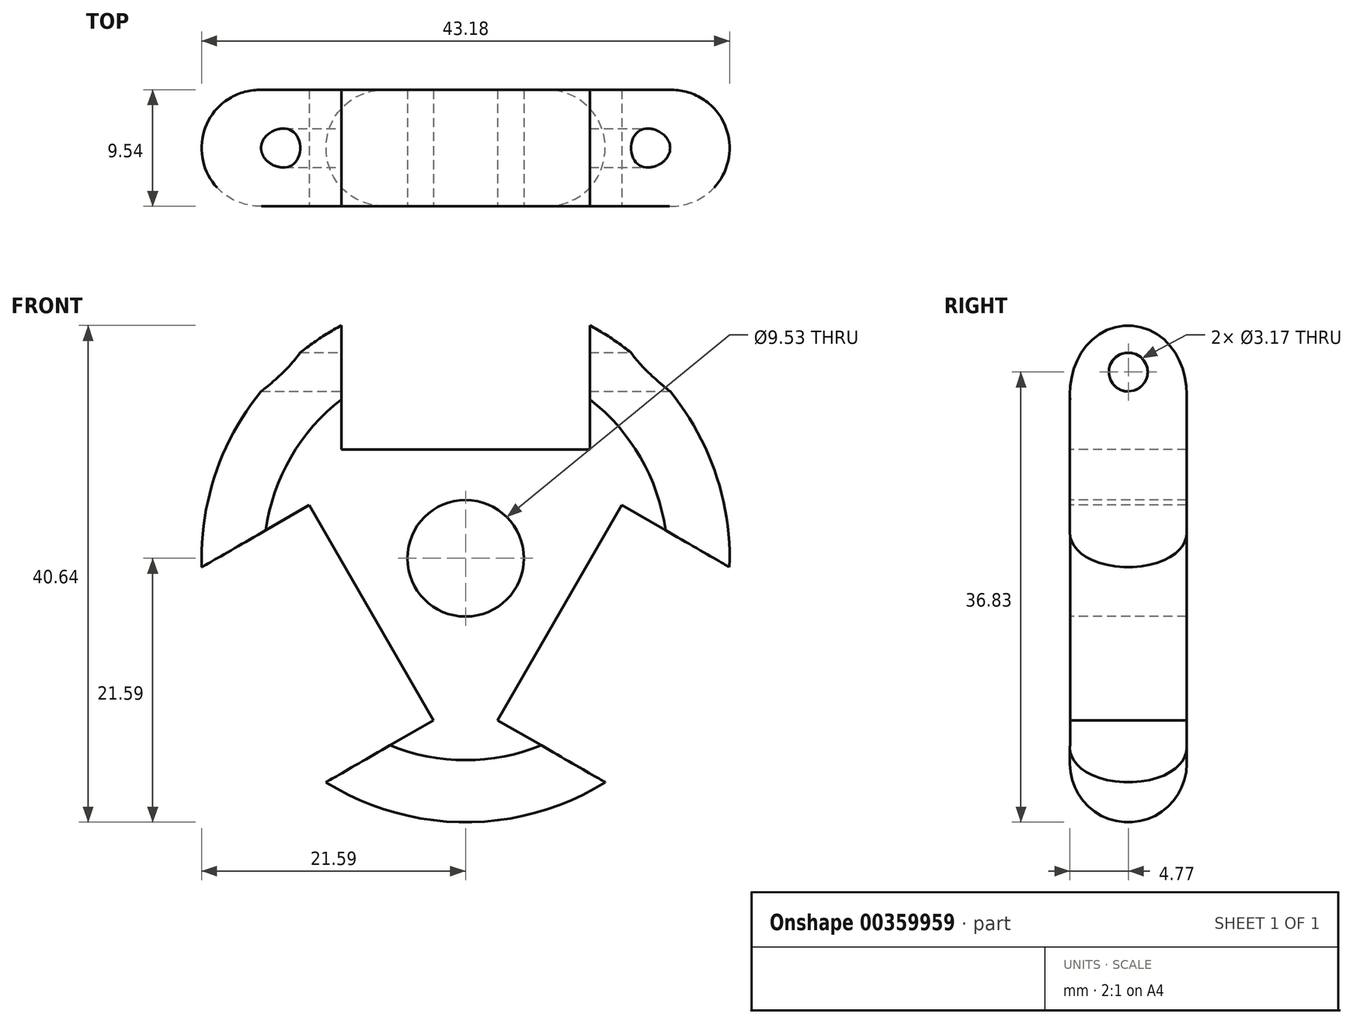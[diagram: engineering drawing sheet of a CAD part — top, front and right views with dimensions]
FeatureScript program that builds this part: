
annotation { "Feature Type Name" : "Feature", "Feature Type Description" : "" }
export const myFeature = defineFeature(function(context is Context, id is Id, definition is map)
    precondition{}
    {
        {
            var Q0;
            Q0=qCreatedBy(makeId("Right.planeOp"),FACE);
            var sketch = newSketch(context, id + "F0", { "sketchPlane" : qUnion([Q0])});
            skLineSegment(sketch, "E0", {"start": v(0, 0) * mm, "end": v(4.76, 0) * mm});
            skLineSegment(sketch, "E1", {"start": v(4.76, 0) * mm, "end": v(4.76, 16.51) * mm});
            skLineSegment(sketch, "E2", {"start": v(0, 0) * mm, "end": v(-4.76, 0) * mm});
            skLineSegment(sketch, "E3", {"start": v(-4.76, 0) * mm, "end": v(-4.76, 16.51) * mm});
            skArc(sketch, "E4", {"start": v(4.76, 16.51) * mm, "mid": v(0, 21.59) * mm, "end": v(-4.76, 16.51) * mm});
            skSolve(sketch);
        }
        {
            var Q0;
            Q0=makeQuery(id+"F0.imprint","IMPRINT",FACE,{"disambiguationData":[TD([[makeQuery(id+"F0.imprint","IMPRINT",EDGE,{"derivedFrom":sQuery(id+"F0.wireOp",EDGE,"E0")}),1.0]])]});
            var Q1;
            Q1=sQuery(id+"F0.wireOp",EDGE,"E2");
            revolve(context, id + "F1", {"entities" : qUnion([Q0]), "axis" : qUnion([Q1]), "revolveType" : RevolveType.FULL});
        }
        {
            var Q0;
            Q0=qCreatedBy(makeId("Front.planeOp"),FACE);
            var sketch = newSketch(context, id + "F2", { "sketchPlane" : qUnion([Q0])});
            skCircle(sketch, "E5", {"center": v(0, 0) * mm, "radius": 4.76 * mm});
            skLineSegment(sketch, "E6", {"start": v(0, 0) * mm, "end": v(0, 0) * mm});
            skLineSegment(sketch, "E7", {"start": v(0, 0) * mm, "end": v(18.7, -10.8) * mm, "construction": true});
            skLineSegment(sketch, "E8", {"start": v(0, 0) * mm, "end": v(-18.7, -10.8) * mm, "construction": true});
            skLineSegment(sketch, "E9", {"start": v(0, 0) * mm, "end": v(0, 21.59) * mm, "construction": true});
            skLineSegment(sketch, "E10.bottom", {"start": v(10.16, 8.89) * mm, "end": v(-10.16, 8.89) * mm});
            skLineSegment(sketch, "E10.top", {"start": v(10.16, 34.3) * mm, "end": v(-10.16, 34.3) * mm});
            skLineSegment(sketch, "E10.left", {"start": v(10.16, 8.89) * mm, "end": v(10.16, 34.3) * mm});
            skLineSegment(sketch, "E10.right", {"start": v(-10.16, 8.89) * mm, "end": v(-10.16, 34.3) * mm});
            skPoint(sketch, "E10.middle", {"position": v(0, 21.59) * mm});
            skLineSegment(sketch, "E11.1.0", {"start": v(-34.78, -8.35) * mm, "end": v(-24.62, -25.94) * mm});
            skLineSegment(sketch, "E11.1.1", {"start": v(-12.78, 4.35) * mm, "end": v(-34.78, -8.35) * mm});
            skLineSegment(sketch, "E11.1.2", {"start": v(-12.78, 4.35) * mm, "end": v(-2.62, -13.24) * mm});
            skLineSegment(sketch, "E11.1.3", {"start": v(-2.62, -13.24) * mm, "end": v(-24.62, -25.94) * mm});
            skLineSegment(sketch, "E11.2.0", {"start": v(24.62, -25.94) * mm, "end": v(34.78, -8.35) * mm});
            skLineSegment(sketch, "E11.2.1", {"start": v(2.62, -13.24) * mm, "end": v(24.62, -25.94) * mm});
            skLineSegment(sketch, "E11.2.2", {"start": v(2.62, -13.24) * mm, "end": v(12.78, 4.35) * mm});
            skLineSegment(sketch, "E11.2.3", {"start": v(12.78, 4.35) * mm, "end": v(34.78, -8.35) * mm});
            skSolve(sketch);
        }
        {
            var Q0;
            Q0 = qSketchRegion(id + "F2", true);
            extrude(context, id + "F3", {"entities" : qUnion([Q0]), "operationType" : NewBodyOperationType.REMOVE, "endBound" : BoundingType.THROUGH_ALL, "oppositeDirection" : true, "depth" : 25.4 * mm, "hasSecondDirection" : true, "secondDirectionBound" : SecondDirectionBoundingType.THROUGH_ALL, "secondDirectionOppositeDirection" : false, "secondDirectionDepth" : 25.4 * mm});
        }
        {
            var Q0;
            Q0=qCreatedBy(makeId("Right.planeOp"),FACE);
            var sketch = newSketch(context, id + "F4", { "sketchPlane" : qUnion([Q0])});
            skCircle(sketch, "E12", {"center": v(0, 15.24) * mm, "radius": 1.59 * mm});
            skSolve(sketch);
        }
        {
            var Q0;
            Q0 = qSketchRegion(id + "F4", true);
            extrude(context, id + "F5", {"entities" : qUnion([Q0]), "operationType" : NewBodyOperationType.REMOVE, "endBound" : BoundingType.THROUGH_ALL, "oppositeDirection" : true, "depth" : 25.4 * mm, "hasSecondDirection" : true, "secondDirectionBound" : SecondDirectionBoundingType.THROUGH_ALL, "secondDirectionOppositeDirection" : false, "secondDirectionDepth" : 25.4 * mm});
        }
        {
            var Q0;
            Q0=qCreatedBy(makeId("Top.planeOp"),FACE);
            var sketch = newSketch(context, id + "F6", { "sketchPlane" : qUnion([Q0])});
            skLineSegment(sketch, "E13", {"start": v(0, -8.38) * mm, "end": v(0, 9.12) * mm, "construction": true});
            skSolve(sketch);
        }
    });
